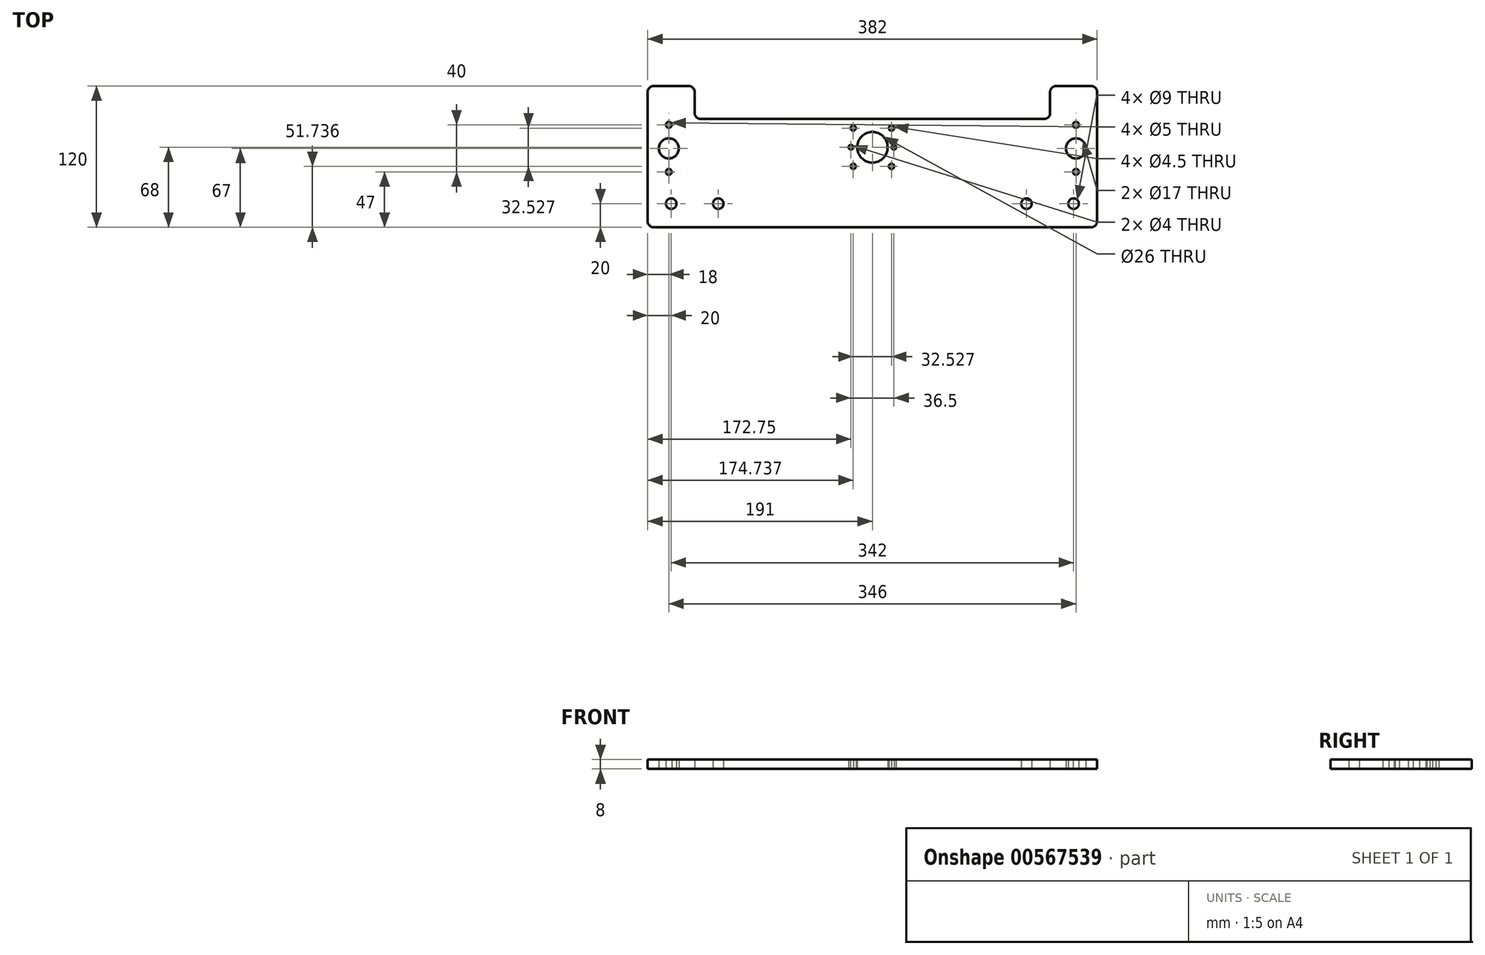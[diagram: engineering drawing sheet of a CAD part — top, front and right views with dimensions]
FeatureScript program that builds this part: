
annotation { "Feature Type Name" : "Feature", "Feature Type Description" : "" }
export const myFeature = defineFeature(function(context is Context, id is Id, definition is map)
    precondition{}
    {
        {
            var Q0;
            Q0=qCreatedBy(makeId("Top.planeOp"),FACE);
            var sketch = newSketch(context, id + "F0", { "sketchPlane" : qUnion([Q0])});
            skLineSegment(sketch, "E0", {"start": v(0, 0) * mm, "end": v(382, 0) * mm});
            skLineSegment(sketch, "E1", {"start": v(382, 0) * mm, "end": v(382, 120) * mm});
            skLineSegment(sketch, "E2", {"start": v(382, 120) * mm, "end": v(342, 120) * mm});
            skLineSegment(sketch, "E3", {"start": v(342, 120) * mm, "end": v(342, 92) * mm});
            skLineSegment(sketch, "E4", {"start": v(342, 92) * mm, "end": v(40, 92) * mm});
            skLineSegment(sketch, "E5", {"start": v(40, 92) * mm, "end": v(40, 120) * mm});
            skLineSegment(sketch, "E6", {"start": v(40, 120) * mm, "end": v(0, 120) * mm});
            skLineSegment(sketch, "E7", {"start": v(0, 120) * mm, "end": v(0, 0) * mm});
            skCircle(sketch, "E8", {"center": v(20, 20) * mm, "radius": 4.5 * mm});
            skCircle(sketch, "E9", {"center": v(60, 20) * mm, "radius": 4.5 * mm});
            skLineSegment(sketch, "E10", {"start": v(191, 92) * mm, "end": v(191, 0) * mm, "construction": true});
            skCircle(sketch, "E11.MirrorC", {"center": v(322, 20) * mm, "radius": 4.5 * mm});
            skCircle(sketch, "E12.MirrorC", {"center": v(362, 20) * mm, "radius": 4.5 * mm});
            skCircle(sketch, "E13", {"center": v(18, 87) * mm, "radius": 2.5 * mm});
            skCircle(sketch, "E14", {"center": v(18, 47) * mm, "radius": 2.5 * mm});
            skCircle(sketch, "E15", {"center": v(18, 67) * mm, "radius": 8.5 * mm});
            skLineSegment(sketch, "E16", {"start": v(18, 87) * mm, "end": v(18, 47) * mm, "construction": true});
            skCircle(sketch, "E17.MirrorC", {"center": v(364, 47) * mm, "radius": 2.5 * mm});
            skCircle(sketch, "E18.MirrorC", {"center": v(364, 67) * mm, "radius": 8.5 * mm});
            skCircle(sketch, "E19.MirrorC", {"center": v(364, 87) * mm, "radius": 2.5 * mm});
            skCircle(sketch, "E20", {"center": v(191, 68) * mm, "radius": 13 * mm});
            skCircle(sketch, "E21", {"center": v(191, 68) * mm, "radius": 23 * mm, "construction": true});
            skLineSegment(sketch, "E22.bottom", {"start": v(207.26, 84.26) * mm, "end": v(174.74, 84.26) * mm, "construction": true});
            skLineSegment(sketch, "E22.top", {"start": v(207.26, 51.74) * mm, "end": v(174.74, 51.74) * mm, "construction": true});
            skLineSegment(sketch, "E22.left", {"start": v(207.26, 84.26) * mm, "end": v(207.26, 51.74) * mm, "construction": true});
            skLineSegment(sketch, "E22.right", {"start": v(174.74, 84.26) * mm, "end": v(174.74, 51.74) * mm, "construction": true});
            skCircle(sketch, "E23", {"center": v(174.74, 84.26) * mm, "radius": 2.25 * mm});
            skCircle(sketch, "E24", {"center": v(207.26, 84.26) * mm, "radius": 2.25 * mm});
            skCircle(sketch, "E25", {"center": v(207.26, 51.74) * mm, "radius": 2.25 * mm});
            skCircle(sketch, "E26", {"center": v(174.74, 51.74) * mm, "radius": 2.25 * mm});
            skCircle(sketch, "E27", {"center": v(209.25, 68) * mm, "radius": 2 * mm});
            skCircle(sketch, "E28", {"center": v(172.75, 68) * mm, "radius": 2 * mm});
            skLineSegment(sketch, "E29", {"start": v(191, 0) * mm, "end": v(191, -7.1) * mm, "construction": true});
            skSolve(sketch);
        }
        {
            var Q0;
            Q0=makeQuery(id+"F0.imprint","IMPRINT",FACE,{"disambiguationData":[TD([[makeQuery(id+"F0.imprint","IMPRINT",EDGE,{"derivedFrom":sQuery(id+"F0.wireOp",EDGE,"E0")}),1.0]])]});
            extrude(context, id + "F1", {"entities" : qUnion([Q0]), "depth" : 8 * mm, "offsetDistance" : 25 * mm});
        }
        {
            var Q0;
            Q0 = qSketchRegion(id + "F0", true);
            extrude(context, id + "F2", {"entities" : qUnion([Q0]), "operationType" : NewBodyOperationType.REMOVE, "oppositeDirection" : true, "depth" : 25 * mm, "offsetDistance" : 25 * mm});
        }
        {
            var Q0;
            Q0=makeQuery(id+"F1.opExtrude","SWEPT_EDGE",EDGE,{"disambiguationData":[OSD([sQuery(id+"F0.wireOp",EDGE,"E0"),sQuery(id+"F0.wireOp",EDGE,"E1")])]});
            var Q1;
            Q1=makeQuery(id+"F1.opExtrude","SWEPT_EDGE",EDGE,{"disambiguationData":[OSD([sQuery(id+"F0.wireOp",EDGE,"E1"),sQuery(id+"F0.wireOp",EDGE,"E2")])]});
            var Q2;
            Q2=makeQuery(id+"F1.opExtrude","SWEPT_EDGE",EDGE,{"disambiguationData":[OSD([sQuery(id+"F0.wireOp",EDGE,"E2"),sQuery(id+"F0.wireOp",EDGE,"E3")])]});
            var Q3;
            Q3=makeQuery(id+"F1.opExtrude","SWEPT_EDGE",EDGE,{"disambiguationData":[OSD([sQuery(id+"F0.wireOp",EDGE,"E3"),sQuery(id+"F0.wireOp",EDGE,"E4")])]});
            var Q4;
            Q4=makeQuery(id+"F1.opExtrude","SWEPT_EDGE",EDGE,{"disambiguationData":[OSD([sQuery(id+"F0.wireOp",EDGE,"E4"),sQuery(id+"F0.wireOp",EDGE,"E5")])]});
            var Q5;
            Q5=makeQuery(id+"F1.opExtrude","SWEPT_EDGE",EDGE,{"disambiguationData":[OSD([sQuery(id+"F0.wireOp",EDGE,"E5"),sQuery(id+"F0.wireOp",EDGE,"E6")])]});
            var Q6;
            Q6=makeQuery(id+"F1.opExtrude","SWEPT_EDGE",EDGE,{"disambiguationData":[OSD([sQuery(id+"F0.wireOp",EDGE,"E6"),sQuery(id+"F0.wireOp",EDGE,"E7")])]});
            var Q7;
            Q7=makeQuery(id+"F1.opExtrude","SWEPT_EDGE",EDGE,{"disambiguationData":[OSD([sQuery(id+"F0.wireOp",EDGE,"E0"),sQuery(id+"F0.wireOp",EDGE,"E7")])]});
            fillet(context, id + "F3", {"entities" : qUnion([Q0, Q1, Q2, Q3, Q4, Q5, Q6, Q7]), "radius" : 5 * mm, "tangentPropagation" : true, "allowEdgeOverflow" : false});
        }
    });
